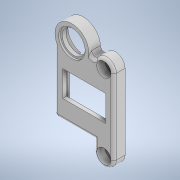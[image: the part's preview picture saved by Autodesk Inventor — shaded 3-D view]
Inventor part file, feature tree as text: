
AUTODESK INVENTOR PART (.ipt)
format: ipt  version: 2020.2 (Build 242310000, 310)  size: 291,328 bytes
history: native  units: mm
features: extrude x7, sketch x7, fillet x2
ambient origin geometry x8: Origin, YZ Plane, XZ Plane, XY Plane, X Axis, Y Axis, Z Axis, Center Point
bodies: Volumenkörper1 (feature_tree)
feature tree (16):
  extrude  "Extrusion1"  Depth=11.2mm
  extrude  "Extrusion2"  Depth=13.4mm
  extrude  "Extrusion3"  Depth=6.8mm
  fillet  "Rundung1"  Radius=6.0mm
  fillet  "Rundung2"  Radius=25.4mm
  extrude  "Extrusion4"  Depth=4.0mm TaperAngle=0.0deg
  extrude  "Extrusion5"  Depth=1.5mm
  extrude  "Extrusion6"  Depth=9.0mm
  extrude  "Extrusion7"  Depth=2.0mm
  sketch  "Skizze1"  dims[d0=22.4mm d1=11.2mm]
  sketch  "Skizze2"  dims[d2=30.4mm d3=15.2mm d4=13.4mm]
  sketch  "Skizze3"  dims[d5=6.7mm d8=6.8mm d9=6.0mm d10=0.0mm d11=25.4mm]
  sketch  "Skizze4"  dims[d12=17.6mm d15=4.0mm d16=0.0mm]
  sketch  "Skizze5"  dims[d19=1.5mm d20=1.5mm]
  sketch  "Skizze6"  dims[d21=2.2mm d22=0.0mm d24=9.0mm]
  sketch  "Skizze7"  dims[d25=4.5mm d26=12.0mm d27=6.0mm d28=2.8mm d29=2.0mm d30=1.5mm d31=1.5mm d32=12.0mm d33=17.6mm d34=7.0mm d35=8.8mm d36=10.0mm d37=3.5mm d38=4.0mm d39=4.6mm d40=4.6mm d41=10.0mm d42=3.5mm d43=30.0mm d44=6.4mm d45=12.7mm d46=4.9mm d47=7.4mm d48=7.4mm d49=4.2mm d50=0.0mm d51=16.2mm d52=3.0mm d53=0.0mm d54=1.2mm d55=27.8mm d56=2.0mm d57=0.0mm d58=13.8mm d59=1.0mm d60=0.0mm d61=9.8mm d62=15.2mm d65=5.0mm d66=39.0mm d67=17.0mm]
